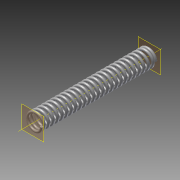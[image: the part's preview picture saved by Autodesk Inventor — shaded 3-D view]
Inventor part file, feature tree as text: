
AUTODESK INVENTOR PART (.ipt)
format: ipt  version: 2014 (Build 180170000, 170)  size: 1,121,792 bytes
history: native  units: in
note: dims shown in document units (in); Inventor stores cm internally (conversion verified against a paired STEP export)
features: other x3, plane x2, imported_body x1
ambient origin geometry x8: Origin, YZ Plane, XZ Plane, XY Plane, X Axis, Y Axis, Z Axis, Center Point
bodies: Body1 (feature_tree)
feature tree (6):
  parser-record x1  (decoder bookkeeping rows leaked as tree rows — omitted from the tree; the rows remain in map.json)
  other  "9657K213 (1)1"
  plane  "Work Plane2"
  other  "Work Axis1"
  imported_body  "Base1"
  plane  "Work Plane1"
